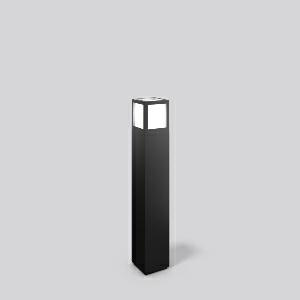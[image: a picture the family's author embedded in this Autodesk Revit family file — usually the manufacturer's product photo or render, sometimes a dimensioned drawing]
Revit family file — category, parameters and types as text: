
# Revit family: hb_205_611978_0031_9fd1
name_source: partatom
category: Lighting Fixtures
units: mm (PartAtom-declared; Revit-internal decimal feet)

## family parameters
Cut with Voids When Loaded = No
Host = Face
Light Source = No
Part Type = Normal
Room Calculation Point = No
Round Connector Dimension = Use Diameter
Shared = No

## types (1)
- HB 205 (1 x LED Modul 830, 390 lm, 3000)
    Apparent Load = 12 VA
    CIE Flux Codes = 10 34 65 40 100
    Color Rendering = 80
    Color Temperature = 3000
    Default Elevation = 1800 mm
    Description = Series: HB 205
Bollard for socket mounting. Housing: die-cast aluminium, powder-coated. Diffuser: plastic (polycarbonate), opal. Driver integrated. 
Colour: anthracite metallic (DB703)
Length: 108 mm
Width: 108 mm
Height: 650 mm
Lamp: LED
System power: 12 W
Rated luminous flux: 390 lm
Luminous efficiency: 33 lm/W
Control gear: Regulated power supply
Protection class: I
Type of protection: IP 54
    Height = 650 mm
    Lamp = 1 x LED Modul 830
    Lamp Light Flux = 390 lm
    Lamp count = 1
    Length = 108 mm
    Lifetime = 50000 h
    Luminous efficacy = 33 lm/W
    Manufacturer = RZB
    ModVariant = No
    Model = 611978.0031
    Mounting Place = Floor
    Mounting Type = Freestanding
    Number of Poles = 1
    OnlyDefault = Yes
    Power Factor = 1
    Product Name = HB 205
    Product group = Bollards
    ProductGroupID = 1351
    Protection Class = Protection class I
    Protection Degree = IP 54
    RLX_Detail_Level = 1
    RLX_Emergency_Light_Flux = 0 lm
    RLX_Emergency_Type = 0
    RLX_Emergency_Type_DB = No
    RlxData = <blob elided: 12657 chars, md5=9f71a55a>
    Socket = socket
    Standby Power = 0 W
    System Light Flux = 390 lm
    System Power = 12 W
    Type Comments = Product without accessories
    Type Image = 611978.0031.jpg
    URL = http://relux.com
    VarID = ---
    Voltage = 0 V
    Weight = 0.00 kg
    Width = 108 mm

## geometry (parser evidence)
native form markers: Sweep x9
no freeform markers — native parametric forms only
